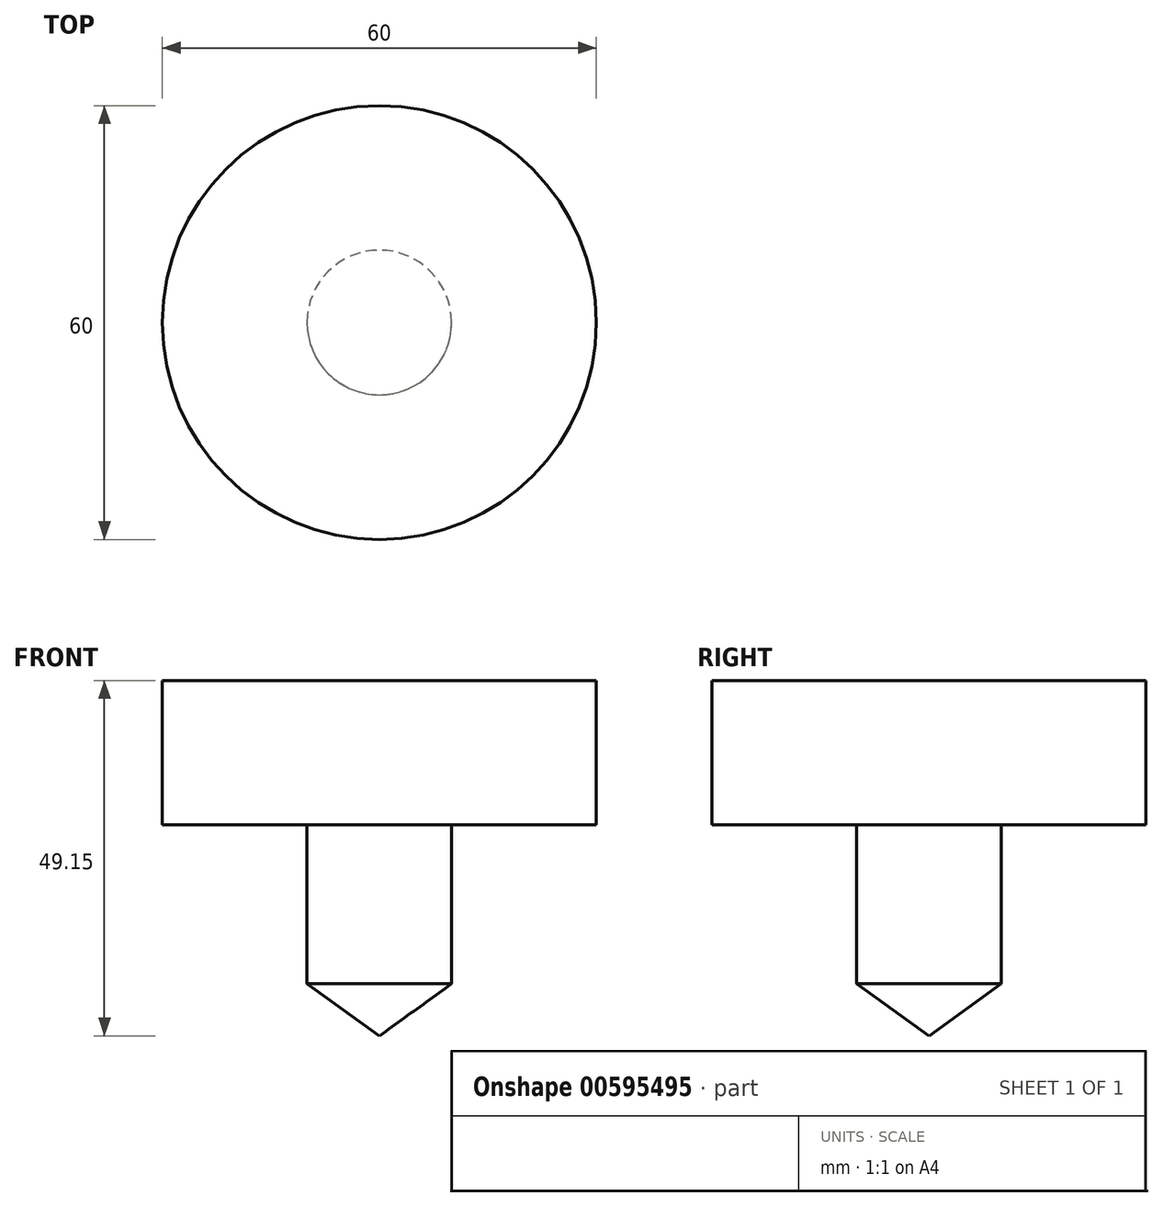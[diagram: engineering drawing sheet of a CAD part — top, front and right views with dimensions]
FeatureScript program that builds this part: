
annotation { "Feature Type Name" : "Feature", "Feature Type Description" : "" }
export const myFeature = defineFeature(function(context is Context, id is Id, definition is map)
    precondition{}
    {
        {
            var Q0;
            Q0=qCreatedBy(makeId("Front.planeOp"),FACE);
            var sketch = newSketch(context, id + "F0", { "sketchPlane" : qUnion([Q0])});
            skLineSegment(sketch, "E0", {"start": v(0, 0) * mm, "end": v(0, 49.15) * mm});
            skLineSegment(sketch, "E1", {"start": v(0, 49.15) * mm, "end": v(30, 49.15) * mm});
            skLineSegment(sketch, "E2", {"start": v(30, 29.15) * mm, "end": v(30, 49.15) * mm});
            skLineSegment(sketch, "E3", {"start": v(10, 29.15) * mm, "end": v(30, 29.15) * mm});
            skLineSegment(sketch, "E4", {"start": v(10, 29.15) * mm, "end": v(10, 7.18) * mm});
            skLineSegment(sketch, "E5", {"start": v(10, 7.18) * mm, "end": v(0, 0) * mm});
            skSolve(sketch);
        }
        {
            var Q0;
            Q0 = qSketchRegion(id + "F0", true);
            var Q1;
            Q1=sQuery(id+"F0.wireOp",EDGE,"E0");
            revolve(context, id + "F1", {"entities" : qUnion([Q0]), "axis" : qUnion([Q1]), "revolveType" : RevolveType.FULL});
        }
    });
